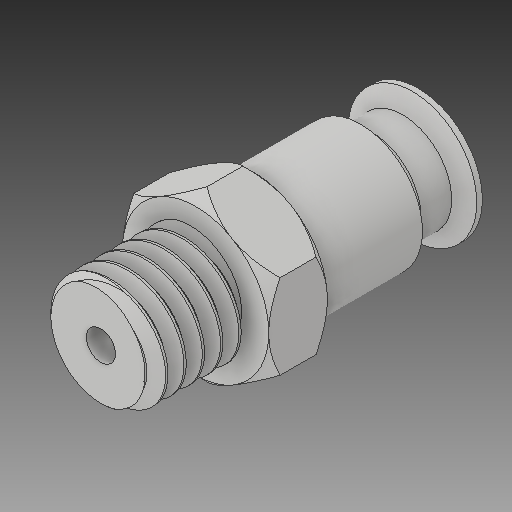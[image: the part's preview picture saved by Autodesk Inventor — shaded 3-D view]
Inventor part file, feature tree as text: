
AUTODESK INVENTOR PART (.ipt)
format: ipt  version: 2019.4 (Build 234330000, 330)  size: 322,048 bytes
history: native  units: in
note: dims shown in document units (in); Inventor stores cm internally (conversion verified against a paired STEP export)
features: revolve x1, boolean_combine x1
ambient origin geometry x8: Origin, YZ Plane, XZ Plane, XY Plane, X Axis, Y Axis, Z Axis, Center Point
bodies: Solid1 (feature_tree), Solid2 (feature_tree)
feature tree (2):
  revolve  "Revolve1"  [1 undecoded]
  boolean_combine  "Combine1"
note: 1 required parameter value undecoded (feature->parameter linkage not recoverable at this tier; creation-order binding heuristic only, values carry confidence <= 0.55)
